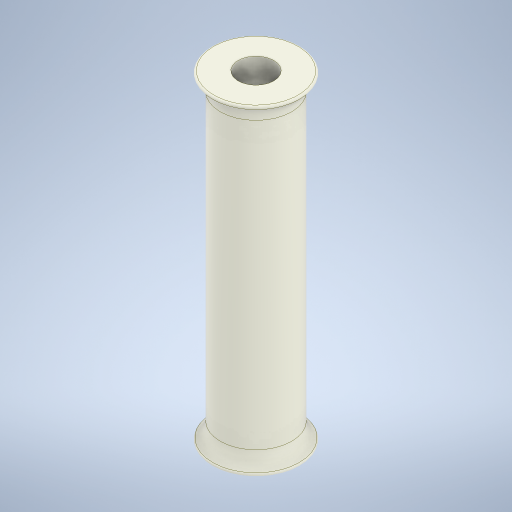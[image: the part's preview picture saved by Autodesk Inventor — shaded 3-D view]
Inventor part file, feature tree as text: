
AUTODESK INVENTOR PART (.ipt)
format: ipt  version: 2024 (Build 280153000, 153)  size: 274,944 bytes
history: native  units: in
note: dims shown in document units (in); Inventor stores cm internally (conversion verified against a paired STEP export)
features: sketch x2, other x1, revolve x1, hole x1
ambient origin geometry x8: Origin, YZ Plane, XZ Plane, XY Plane, X Axis, Y Axis, Z Axis, Center Point
bodies: Body1 (feature_tree)
feature tree (5):
  other  "Main Body"
  revolve  "Revolution1"  [1 undecoded]
  hole  "Hole1"  [1 undecoded]
  sketch  "Sketch1"  dims[d0=0.1969in d1=1.5748in]
  sketch  "Sketch2"  dims[d2=0.1969in d3=0.2953in d4=0.0098in d5=0.0984in d6=0.1969in d7=0.2953in d8=0.0098in d9=90.0deg d10=0.1969in d11=0.2953in d12=0.1476in d13=0.0984in d14=90.0deg d15=0.3937in d16=0.8108in]
note: 2 required parameter values undecoded (feature->parameter linkage not recoverable at this tier; creation-order binding heuristic only, values carry confidence <= 0.55)